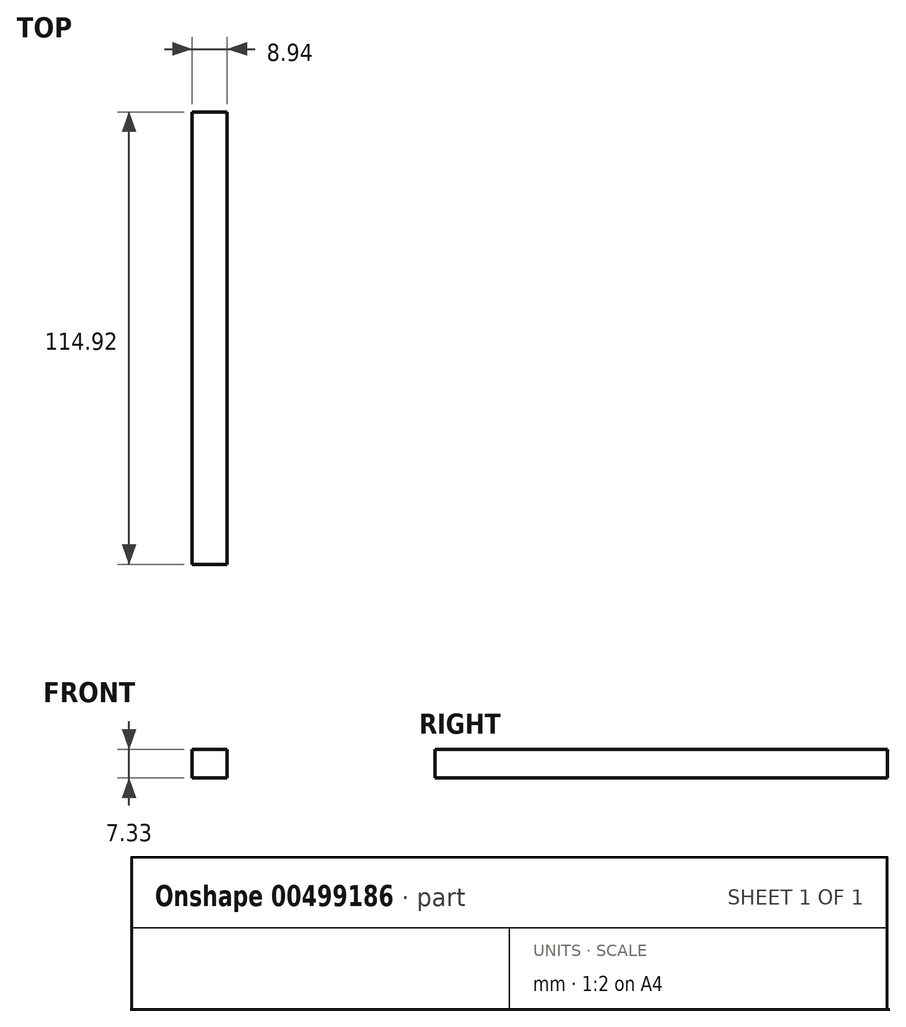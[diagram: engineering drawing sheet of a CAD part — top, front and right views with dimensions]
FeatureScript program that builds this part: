
annotation { "Feature Type Name" : "Feature", "Feature Type Description" : "" }
export const myFeature = defineFeature(function(context is Context, id is Id, definition is map)
    precondition{}
    {
        {
            var Q0;
            Q0=qCreatedBy(makeId("Right.planeOp"),FACE);
            var sketch = newSketch(context, id + "F0", { "sketchPlane" : qUnion([Q0])});
            skLineSegment(sketch, "E0.bottom", {"start": v(0, 46.17) * mm, "end": v(-114.92, 46.17) * mm});
            skLineSegment(sketch, "E0.top", {"start": v(0, 36.25) * mm, "end": v(-114.92, 36.25) * mm});
            skLineSegment(sketch, "E0.left", {"start": v(0, 46.17) * mm, "end": v(0, 36.25) * mm});
            skLineSegment(sketch, "E0.right", {"start": v(-114.92, 46.17) * mm, "end": v(-114.92, 36.25) * mm});
            skSolve(sketch);
        }
        {
            var Q0;
            Q0=sQuery(id+"F0.wireOp",EDGE,"E0.top");
            extrude(context, id + "F1", {"bodyType" : ToolBodyType.SURFACE, "surfaceEntities" : qUnion([Q0]), "oppositeDirection" : true, "depth" : 8.94 * mm});
        }
        {
            var Q0;
            Q0=makeQuery(id+"F1.opExtrude","SWEPT_FACE",FACE,{"disambiguationData":[OSD([sQuery(id+"F0.wireOp",EDGE,"E0.top")])]});
            extrude(context, id + "F2", {"entities" : qUnion([Q0]), "depth" : 7.33 * mm});
        }
    });
